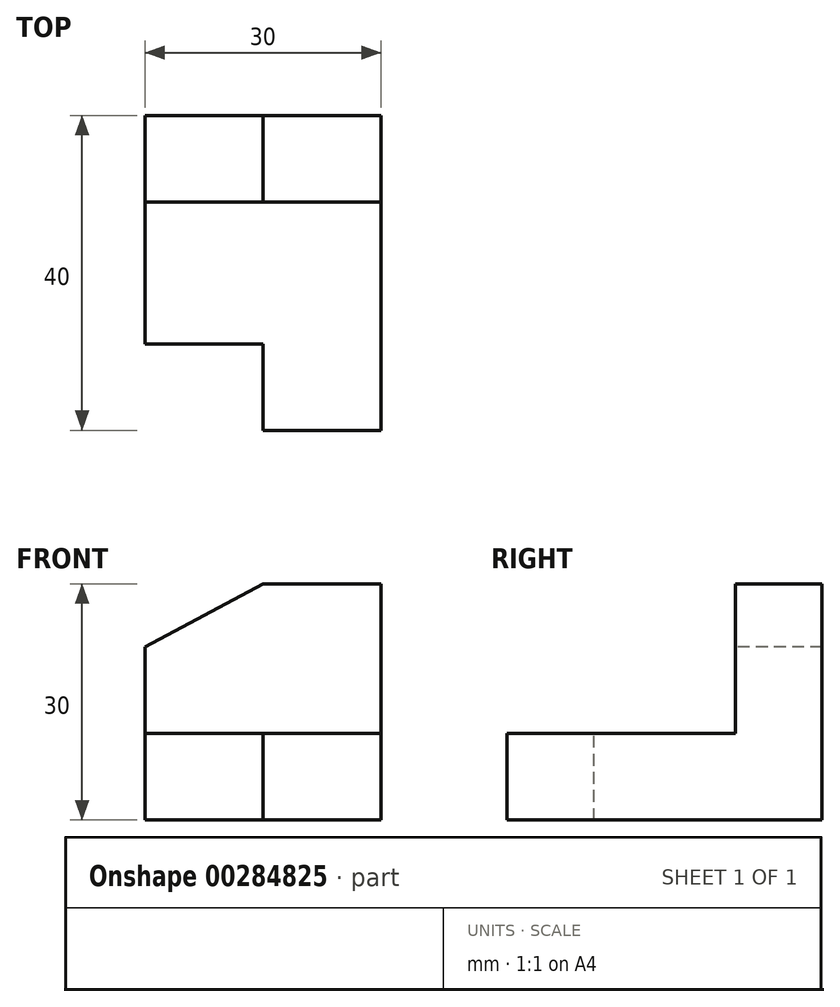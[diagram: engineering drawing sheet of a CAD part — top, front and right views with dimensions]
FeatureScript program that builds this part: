
annotation { "Feature Type Name" : "Feature", "Feature Type Description" : "" }
export const myFeature = defineFeature(function(context is Context, id is Id, definition is map)
    precondition{}
    {
        {
            var Q0;
            Q0=qCreatedBy(makeId("Front.planeOp"),FACE);
            var sketch = newSketch(context, id + "F0", { "sketchPlane" : qUnion([Q0])});
            skLineSegment(sketch, "E0.bottom", {"start": v(0, 0) * mm, "end": v(40, 0) * mm});
            skLineSegment(sketch, "E0.top", {"start": v(0, 30) * mm, "end": v(40, 30) * mm});
            skLineSegment(sketch, "E0.left", {"start": v(0, 0) * mm, "end": v(0, 30) * mm});
            skLineSegment(sketch, "E0.right", {"start": v(40, 0) * mm, "end": v(40, 30) * mm});
            skLineSegment(sketch, "E1.bottom", {"start": v(40, 30) * mm, "end": v(11, 30) * mm});
            skLineSegment(sketch, "E1.top", {"start": v(40, 11) * mm, "end": v(11, 11) * mm});
            skLineSegment(sketch, "E1.left", {"start": v(40, 30) * mm, "end": v(40, 11) * mm});
            skLineSegment(sketch, "E1.right", {"start": v(11, 30) * mm, "end": v(11, 11) * mm});
            skSolve(sketch);
        }
        {
            var Q0;
            Q0=makeQuery(id+"F0.imprint","IMPRINT",FACE,{"disambiguationData":[TD([[makeQuery(id+"F0.imprint","IMPRINT",EDGE,{"derivedFrom":sQuery(id+"F0.wireOp",EDGE,"E0.bottom")}),1.0]])]});
            extrude(context, id + "F1", {"entities" : qUnion([Q0]), "depth" : 30 * mm});
        }
        {
            var Q0;
            Q0=makeQuery(id+"F1.opExtrude","SWEPT_FACE",FACE,{"disambiguationData":[OSD([sQuery(id+"F0.wireOp",EDGE,"E1.top")])]});
            var sketch = newSketch(context, id + "F2", { "sketchPlane" : qUnion([Q0])});
            skPoint(sketch, "E2.oppositeSnap0", {"position": v(40, -15) * mm});
            skLineSegment(sketch, "E2.bottom", {"start": v(40, -30) * mm, "end": v(29, -30) * mm});
            skLineSegment(sketch, "E2.top", {"start": v(40, -15) * mm, "end": v(29, -15) * mm});
            skLineSegment(sketch, "E2.left", {"start": v(40, -30) * mm, "end": v(40, -15) * mm});
            skLineSegment(sketch, "E2.right", {"start": v(29, -30) * mm, "end": v(29, -15) * mm});
            skSolve(sketch);
        }
        {
            var Q0;
            Q0=qSketchRegion(id+"F2",true);
            var Q1;
            Q1=makeQuery(id+"F1.opExtrude","CAP_VERTEX",VERTEX,{"disambiguationData":[OSD([sQuery(id+"F0.wireOp",EDGE,"E0.bottom"),sQuery(id+"F0.wireOp",EDGE,"E0.right")])],"isStart":false});
            extrude(context, id + "F3", {"entities" : qUnion([Q0]), "operationType" : NewBodyOperationType.REMOVE, "endBound" : BoundingType.UP_TO_VERTEX, "oppositeDirection" : true, "endBoundEntityVertex" : qUnion([Q1]), "depth" : 25 * mm});
        }
        {
            var Q0;
            Q0=makeQuery(id+"F1.opExtrude","SWEPT_FACE",FACE,{"disambiguationData":[OSD([sQuery(id+"F0.wireOp",EDGE,"E1.right")])]});
            var sketch = newSketch(context, id + "F4", { "sketchPlane" : qUnion([Q0])});
            skPoint(sketch, "E3.oppositeSnap0", {"position": v(-15, 30) * mm});
            skLineSegment(sketch, "E3.bottom", {"start": v(-30, 30) * mm, "end": v(-15, 30) * mm});
            skLineSegment(sketch, "E3.top", {"start": v(-30, 22) * mm, "end": v(-15, 22) * mm});
            skLineSegment(sketch, "E3.left", {"start": v(-30, 30) * mm, "end": v(-30, 22) * mm});
            skLineSegment(sketch, "E3.right", {"start": v(-15, 30) * mm, "end": v(-15, 22) * mm});
            skSolve(sketch);
        }
        {
            var Q0;
            Q0=qSketchRegion(id+"F4",true);
            var Q1;
            Q1=makeQuery(id+"F1.opExtrude","CAP_VERTEX",VERTEX,{"disambiguationData":[OSD([sQuery(id+"F0.wireOp",EDGE,"E0.top"),sQuery(id+"F0.wireOp",EDGE,"E0.left")])],"isStart":false});
            extrude(context, id + "F5", {"entities" : qUnion([Q0]), "operationType" : NewBodyOperationType.REMOVE, "endBound" : BoundingType.UP_TO_VERTEX, "oppositeDirection" : true, "endBoundEntityVertex" : qUnion([Q1]), "depth" : 25 * mm});
        }
        {
            var Q0;
            Q0=makeQuery(id+"F1.opExtrude","SWEPT_BODY",BODY,{"disambiguationData":[OSD([sQuery(id+"F0.wireOp",EDGE,"E0.bottom"),sQuery(id+"F0.wireOp",EDGE,"E0.top"),sQuery(id+"F0.wireOp",EDGE,"E0.left"),sQuery(id+"F0.wireOp",EDGE,"E0.right"),sQuery(id+"F0.wireOp",EDGE,"E1.top"),sQuery(id+"F0.wireOp",EDGE,"E1.right")])]});
            var Q1;
            Q1=makeQuery(id+"F1.opExtrude","CAP_EDGE",EDGE,{"disambiguationData":[OSD([sQuery(id+"F0.wireOp",EDGE,"E0.left")])],"isStart":true});
            transform(context, id + "F6", {"entities" : qUnion([Q0]), "transformType" : TransformType.ROTATION, "transformAxis" : qUnion([Q1]), "angle" : 90 * degree, "oppositeDirection" : true, "makeCopy" : false});
        }
        {
            var Q0;
            Q0=makeQuery(id+"F1.opExtrude","SWEPT_FACE",FACE,{"disambiguationData":[OSD([sQuery(id+"F0.wireOp",EDGE,"E1.right")])]});
            var sketch = newSketch(context, id + "F7", { "sketchPlane" : qUnion([Q0])});
            skLineSegment(sketch, "E4", {"start": v(-15, 30) * mm, "end": v(-30, 22) * mm});
            skSolve(sketch);
        }
        {
            var Q0;
            Q0=makeQuery(id+"F7.imprint","IMPRINT",FACE,{"disambiguationData":[TD([[makeQuery(id+"F7.imprint","IMPRINT",EDGE,{"derivedFrom":sQuery(id+"F7.wireOp",EDGE,"E4")}),1.0]])]});
            var Q1;
            Q1=makeQuery(id+"F5.boolean.opBoolean","COPY",VERTEX,{"derivedFrom":makeQuery(id+"F5.opExtrude","CAP_VERTEX",VERTEX,{"disambiguationData":[OSD([sQuery(id+"F0.wireOp",EDGE,"E0.top"),sQuery(id+"F0.wireOp",EDGE,"E1.bottom"),sQuery(id+"F0.wireOp",EDGE,"E1.right"),sQuery(id+"F4.wireOp",EDGE,"E3.bottom"),sQuery(id+"F4.wireOp",EDGE,"E3.right"),dummyQuery(id+"F5.vertexPlane.planeOp",FACE)])],"isStart":false})});
            extrude(context, id + "F8", {"entities" : qUnion([Q0]), "operationType" : NewBodyOperationType.ADD, "endBound" : BoundingType.UP_TO_VERTEX, "oppositeDirection" : true, "endBoundEntityVertex" : qUnion([Q1]), "depth" : 25 * mm});
        }
    });
